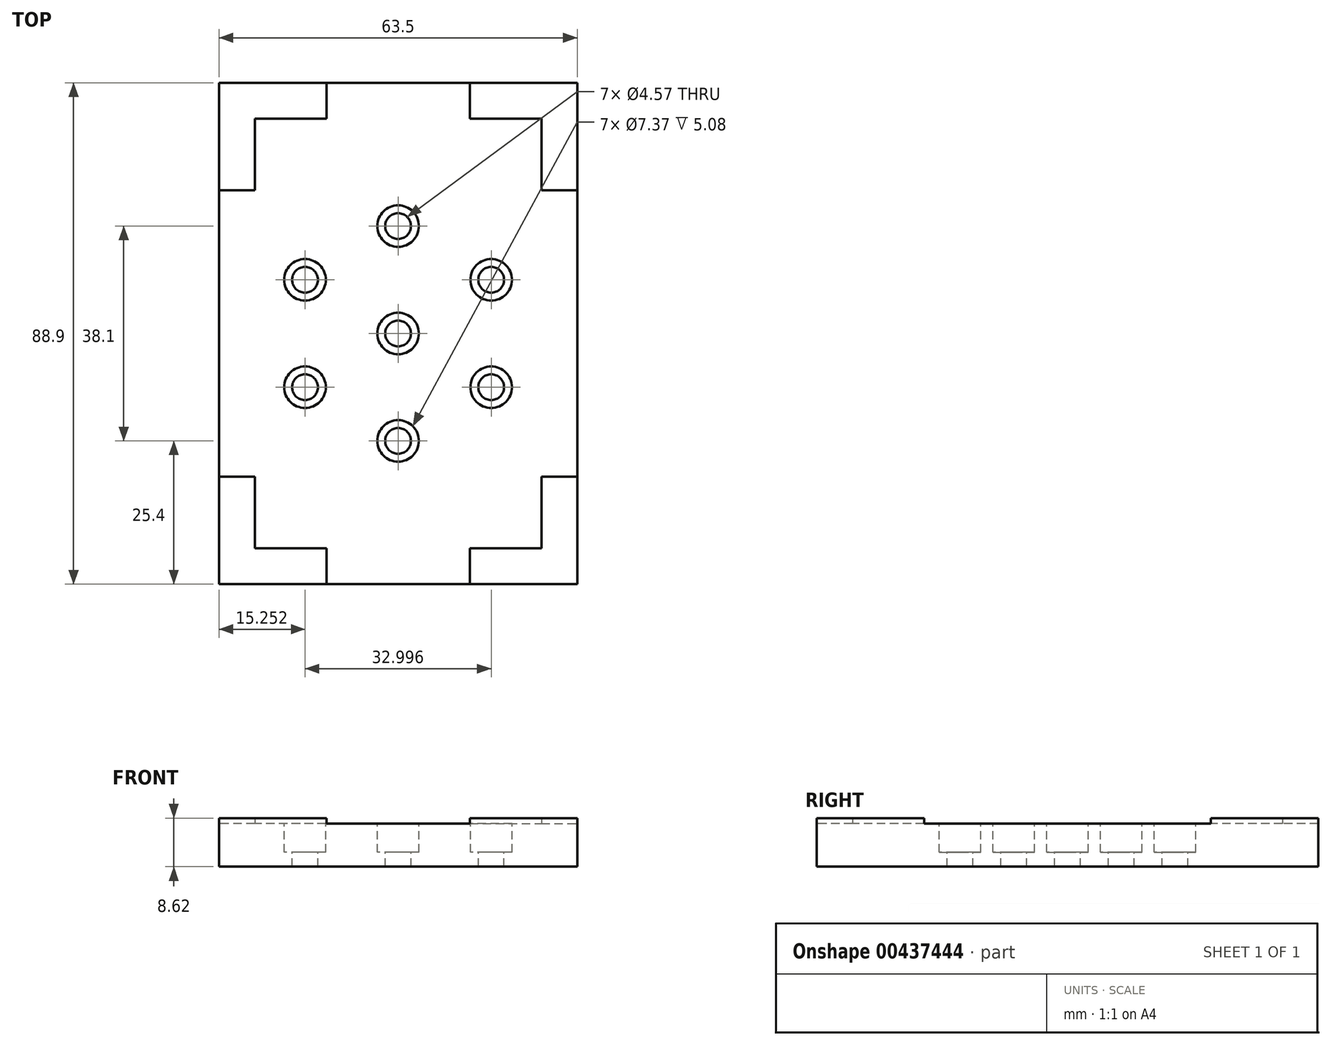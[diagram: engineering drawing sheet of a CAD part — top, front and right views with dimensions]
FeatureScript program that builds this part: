
annotation { "Feature Type Name" : "Feature", "Feature Type Description" : "" }
export const myFeature = defineFeature(function(context is Context, id is Id, definition is map)
    precondition{}
    {
        {
            var Q0;
            Q0=qCreatedBy(makeId("Top.planeOp"),FACE);
            var sketch = newSketch(context, id + "F0", { "sketchPlane" : qUnion([Q0])});
            skLineSegment(sketch, "E0.bottom", {"start": v(0, 0) * mm, "end": v(63.5, 0) * mm});
            skLineSegment(sketch, "E0.top", {"start": v(0, 88.9) * mm, "end": v(63.5, 88.9) * mm});
            skLineSegment(sketch, "E0.left", {"start": v(0, 0) * mm, "end": v(0, 88.9) * mm});
            skLineSegment(sketch, "E0.right", {"start": v(63.5, 0) * mm, "end": v(63.5, 88.9) * mm});
            skSolve(sketch);
        }
        {
            var Q0;
            Q0=makeQuery(id+"F0.imprint","IMPRINT",FACE,{"disambiguationData":[TD([[makeQuery(id+"F0.imprint","IMPRINT",EDGE,{"derivedFrom":sQuery(id+"F0.wireOp",EDGE,"E0.bottom")}),1.0]])]});
            extrude(context, id + "F1", {"entities" : qUnion([Q0]), "depth" : 7.62 * mm});
        }
        {
            var Q0;
            Q0=makeQuery(id+"F1.opExtrude","CAP_FACE",FACE,{"disambiguationData":[OSD([sQuery(id+"F0.wireOp",EDGE,"E0.bottom"),sQuery(id+"F0.wireOp",EDGE,"E0.top"),sQuery(id+"F0.wireOp",EDGE,"E0.left"),sQuery(id+"F0.wireOp",EDGE,"E0.right")])],"isStart":false});
            var sketch = newSketch(context, id + "F2", { "sketchPlane" : qUnion([Q0])});
            skCircle(sketch, "E1", {"center": v(31.75, 44.45) * mm, "radius": 2.29 * mm});
            skCircle(sketch, "E2", {"center": v(31.75, 63.5) * mm, "radius": 2.29 * mm});
            skCircle(sketch, "E3", {"center": v(31.75, 25.4) * mm, "radius": 2.29 * mm});
            skCircle(sketch, "E4", {"center": v(48.25, 34.92) * mm, "radius": 2.29 * mm});
            skCircle(sketch, "E5", {"center": v(48.25, 53.98) * mm, "radius": 2.29 * mm});
            skCircle(sketch, "E6", {"center": v(15.25, 53.98) * mm, "radius": 2.29 * mm});
            skCircle(sketch, "E7", {"center": v(15.25, 34.93) * mm, "radius": 2.29 * mm});
            skLineSegment(sketch, "E8", {"start": v(15.25, 34.93) * mm, "end": v(15.25, 53.98) * mm});
            skLineSegment(sketch, "E9", {"start": v(15.25, 53.98) * mm, "end": v(48.25, 53.98) * mm});
            skLineSegment(sketch, "E10", {"start": v(48.25, 34.92) * mm, "end": v(48.25, 53.98) * mm});
            skLineSegment(sketch, "E11", {"start": v(15.25, 34.93) * mm, "end": v(48.25, 34.93) * mm});
            skLineSegment(sketch, "E12", {"start": v(31.75, 44.45) * mm, "end": v(31.75, 63.5) * mm});
            skSolve(sketch);
        }
        {
            var Q0;
            Q0=makeQuery(id+"F2.imprint","IMPRINT",FACE,{"disambiguationData":[TD([[makeQuery(id+"F2.imprint","IMPRINT",EDGE,{"derivedFrom":sQuery(id+"F2.wireOp",EDGE,"E2")}),1.0]])]});
            var Q1;
            Q1=makeQuery(id+"F2.imprint","IMPRINT",FACE,{"disambiguationData":[TD([[makeQuery(id+"F2.imprint","IMPRINT",EDGE,{"derivedFrom":sQuery(id+"F2.wireOp",EDGE,"E3")}),1.0]])]});
            var Q2;
            {var subQ0=sQuery(id+"F2.wireOp",EDGE,"E10");var subQ1=sQuery(id+"F2.wireOp",EDGE,"E4");var subQ2=makeQuery(id+"F2.imprint","INTERSECT",VERTEX,{"derivedFrom":[subQ1,subQ0]});Q2=makeQuery(id+"F2.imprint","IMPRINT",FACE,{"disambiguationData":[TD([[makeQuery(id+"F2.imprint","IMPRINT",EDGE,{"disambiguationData":[TD([[subQ2,-1.0]])],"derivedFrom":subQ1}),1.0]])]});}
            var Q3;
            {var subQ0=sQuery(id+"F2.wireOp",EDGE,"E10");var subQ1=sQuery(id+"F2.wireOp",EDGE,"E4");var subQ2=makeQuery(id+"F2.imprint","INTERSECT",VERTEX,{"derivedFrom":[subQ1,subQ0]});Q3=makeQuery(id+"F2.imprint","IMPRINT",FACE,{"disambiguationData":[TD([[makeQuery(id+"F2.imprint","IMPRINT",EDGE,{"disambiguationData":[TD([[subQ2,1.0]])],"derivedFrom":subQ1}),1.0]])]});}
            var Q4;
            {var subQ0=sQuery(id+"F2.wireOp",EDGE,"E9");var subQ1=sQuery(id+"F2.wireOp",EDGE,"E5");var subQ2=makeQuery(id+"F2.imprint","INTERSECT",VERTEX,{"derivedFrom":[subQ1,subQ0]});Q4=makeQuery(id+"F2.imprint","IMPRINT",FACE,{"disambiguationData":[TD([[makeQuery(id+"F2.imprint","IMPRINT",EDGE,{"disambiguationData":[TD([[subQ2,-1.0]])],"derivedFrom":subQ1}),1.0]])]});}
            var Q5;
            {var subQ0=sQuery(id+"F2.wireOp",EDGE,"E9");var subQ1=sQuery(id+"F2.wireOp",EDGE,"E5");var subQ2=makeQuery(id+"F2.imprint","INTERSECT",VERTEX,{"derivedFrom":[subQ1,subQ0]});Q5=makeQuery(id+"F2.imprint","IMPRINT",FACE,{"disambiguationData":[TD([[makeQuery(id+"F2.imprint","IMPRINT",EDGE,{"disambiguationData":[TD([[subQ2,1.0]])],"derivedFrom":subQ1}),1.0]])]});}
            var Q6;
            {var subQ0=sQuery(id+"F2.wireOp",EDGE,"E8");var subQ1=sQuery(id+"F2.wireOp",EDGE,"E6");var subQ2=makeQuery(id+"F2.imprint","INTERSECT",VERTEX,{"derivedFrom":[subQ1,subQ0]});Q6=makeQuery(id+"F2.imprint","IMPRINT",FACE,{"disambiguationData":[TD([[makeQuery(id+"F2.imprint","IMPRINT",EDGE,{"disambiguationData":[TD([[subQ2,1.0]])],"derivedFrom":subQ1}),1.0]])]});}
            var Q7;
            {var subQ0=sQuery(id+"F2.wireOp",EDGE,"E8");var subQ1=sQuery(id+"F2.wireOp",EDGE,"E6");var subQ2=makeQuery(id+"F2.imprint","INTERSECT",VERTEX,{"derivedFrom":[subQ1,subQ0]});Q7=makeQuery(id+"F2.imprint","IMPRINT",FACE,{"disambiguationData":[TD([[makeQuery(id+"F2.imprint","IMPRINT",EDGE,{"disambiguationData":[TD([[subQ2,-1.0]])],"derivedFrom":subQ1}),1.0]])]});}
            var Q8;
            {var subQ0=sQuery(id+"F2.wireOp",EDGE,"E8");var subQ1=sQuery(id+"F2.wireOp",EDGE,"E7");var subQ2=makeQuery(id+"F2.imprint","INTERSECT",VERTEX,{"derivedFrom":[subQ1,subQ0]});Q8=makeQuery(id+"F2.imprint","IMPRINT",FACE,{"disambiguationData":[TD([[makeQuery(id+"F2.imprint","IMPRINT",EDGE,{"disambiguationData":[TD([[subQ2,1.0]])],"derivedFrom":subQ1}),1.0]])]});}
            var Q9;
            {var subQ0=sQuery(id+"F2.wireOp",EDGE,"E8");var subQ1=sQuery(id+"F2.wireOp",EDGE,"E7");var subQ2=makeQuery(id+"F2.imprint","INTERSECT",VERTEX,{"derivedFrom":[subQ1,subQ0]});Q9=makeQuery(id+"F2.imprint","IMPRINT",FACE,{"disambiguationData":[TD([[makeQuery(id+"F2.imprint","IMPRINT",EDGE,{"disambiguationData":[TD([[subQ2,-1.0]])],"derivedFrom":subQ1}),1.0]])]});}
            var Q10;
            Q10=makeQuery(id+"F2.imprint","IMPRINT",FACE,{"disambiguationData":[TD([[makeQuery(id+"F2.imprint","IMPRINT",EDGE,{"derivedFrom":sQuery(id+"F2.wireOp",EDGE,"E1")}),1.0]])]});
            extrude(context, id + "F3", {"entities" : qUnion([Q0, Q1, Q2, Q3, Q4, Q5, Q6, Q7, Q8, Q9, Q10]), "operationType" : NewBodyOperationType.REMOVE, "oppositeDirection" : true, "depth" : 25.4 * mm});
        }
        {
            var Q0;
            Q0=makeQuery(id+"F1.opExtrude","CAP_FACE",FACE,{"disambiguationData":[OSD([sQuery(id+"F0.wireOp",EDGE,"E0.bottom"),sQuery(id+"F0.wireOp",EDGE,"E0.top"),sQuery(id+"F0.wireOp",EDGE,"E0.left"),sQuery(id+"F0.wireOp",EDGE,"E0.right")])],"isStart":false});
            var sketch = newSketch(context, id + "F4", { "sketchPlane" : qUnion([Q0])});
            skCircle(sketch, "E13", {"center": v(15.25, 34.93) * mm, "radius": 3.68 * mm});
            skCircle(sketch, "E14", {"center": v(15.25, 53.98) * mm, "radius": 3.68 * mm});
            skCircle(sketch, "E15", {"center": v(31.75, 63.5) * mm, "radius": 3.68 * mm});
            skCircle(sketch, "E16", {"center": v(48.25, 53.98) * mm, "radius": 3.68 * mm});
            skCircle(sketch, "E17", {"center": v(48.25, 34.92) * mm, "radius": 3.68 * mm});
            skCircle(sketch, "E18", {"center": v(31.75, 25.4) * mm, "radius": 3.68 * mm});
            skCircle(sketch, "E19", {"center": v(31.75, 44.45) * mm, "radius": 3.68 * mm});
            skSolve(sketch);
        }
        {
            var Q0;
            Q0=makeQuery(id+"F4.imprint","IMPRINT",FACE,{"disambiguationData":[TD([[makeQuery(id+"F4.imprint","IMPRINT",EDGE,{"derivedFrom":sQuery(id+"F4.wireOp",EDGE,"E13")}),1.0]])]});
            var Q1;
            Q1=makeQuery(id+"F4.imprint","IMPRINT",FACE,{"disambiguationData":[TD([[makeQuery(id+"F4.imprint","IMPRINT",EDGE,{"derivedFrom":sQuery(id+"F4.wireOp",EDGE,"E14")}),1.0]])]});
            var Q2;
            Q2=makeQuery(id+"F4.imprint","IMPRINT",FACE,{"disambiguationData":[TD([[makeQuery(id+"F4.imprint","IMPRINT",EDGE,{"derivedFrom":sQuery(id+"F4.wireOp",EDGE,"E15")}),1.0]])]});
            var Q3;
            Q3=makeQuery(id+"F4.imprint","IMPRINT",FACE,{"disambiguationData":[TD([[makeQuery(id+"F4.imprint","IMPRINT",EDGE,{"derivedFrom":sQuery(id+"F4.wireOp",EDGE,"E16")}),1.0]])]});
            var Q4;
            Q4=makeQuery(id+"F4.imprint","IMPRINT",FACE,{"disambiguationData":[TD([[makeQuery(id+"F4.imprint","IMPRINT",EDGE,{"derivedFrom":sQuery(id+"F4.wireOp",EDGE,"E17")}),1.0]])]});
            var Q5;
            Q5=makeQuery(id+"F4.imprint","IMPRINT",FACE,{"disambiguationData":[TD([[makeQuery(id+"F4.imprint","IMPRINT",EDGE,{"derivedFrom":sQuery(id+"F4.wireOp",EDGE,"E18")}),1.0]])]});
            var Q6;
            Q6=makeQuery(id+"F4.imprint","IMPRINT",FACE,{"disambiguationData":[TD([[makeQuery(id+"F4.imprint","IMPRINT",EDGE,{"derivedFrom":sQuery(id+"F4.wireOp",EDGE,"E19")}),1.0]])]});
            extrude(context, id + "F5", {"entities" : qUnion([Q0, Q1, Q2, Q3, Q4, Q5, Q6]), "operationType" : NewBodyOperationType.REMOVE, "oppositeDirection" : true, "depth" : 5.08 * mm});
        }
        {
            var Q0;
            Q0=makeQuery(id+"F1.opExtrude","CAP_FACE",FACE,{"disambiguationData":[OSD([sQuery(id+"F0.wireOp",EDGE,"E0.bottom"),sQuery(id+"F0.wireOp",EDGE,"E0.top"),sQuery(id+"F0.wireOp",EDGE,"E0.left"),sQuery(id+"F0.wireOp",EDGE,"E0.right")])],"isStart":false});
            var sketch = newSketch(context, id + "F6", { "sketchPlane" : qUnion([Q0])});
            skLineSegment(sketch, "E20", {"start": v(0, 19.05) * mm, "end": v(6.35, 19.05) * mm});
            skLineSegment(sketch, "E21", {"start": v(6.35, 19.05) * mm, "end": v(6.35, 6.35) * mm});
            skLineSegment(sketch, "E22", {"start": v(6.35, 6.35) * mm, "end": v(19.05, 6.35) * mm});
            skLineSegment(sketch, "E23", {"start": v(19.05, 6.35) * mm, "end": v(19.05, 0) * mm});
            skLineSegment(sketch, "E24", {"start": v(19.05, 0) * mm, "end": v(44.45, 0) * mm});
            skLineSegment(sketch, "E25", {"start": v(44.45, 0) * mm, "end": v(44.45, 6.35) * mm});
            skLineSegment(sketch, "E26", {"start": v(44.45, 6.35) * mm, "end": v(57.15, 6.35) * mm});
            skLineSegment(sketch, "E27", {"start": v(57.15, 6.35) * mm, "end": v(57.15, 19.05) * mm});
            skLineSegment(sketch, "E28", {"start": v(57.15, 19.05) * mm, "end": v(63.5, 19.05) * mm});
            skLineSegment(sketch, "E29", {"start": v(63.5, 19.05) * mm, "end": v(63.5, 69.85) * mm});
            skLineSegment(sketch, "E30", {"start": v(63.5, 69.85) * mm, "end": v(57.15, 69.85) * mm});
            skLineSegment(sketch, "E31", {"start": v(57.15, 69.85) * mm, "end": v(57.15, 82.55) * mm});
            skLineSegment(sketch, "E32", {"start": v(57.15, 82.55) * mm, "end": v(44.45, 82.55) * mm});
            skLineSegment(sketch, "E33", {"start": v(44.45, 82.55) * mm, "end": v(44.45, 88.9) * mm});
            skLineSegment(sketch, "E34", {"start": v(44.45, 88.9) * mm, "end": v(19.05, 88.9) * mm});
            skLineSegment(sketch, "E35", {"start": v(19.05, 88.9) * mm, "end": v(19.05, 82.55) * mm});
            skLineSegment(sketch, "E36", {"start": v(19.05, 82.55) * mm, "end": v(6.35, 82.55) * mm});
            skLineSegment(sketch, "E37", {"start": v(6.35, 82.55) * mm, "end": v(6.35, 69.85) * mm});
            skLineSegment(sketch, "E38", {"start": v(6.35, 69.85) * mm, "end": v(0, 69.85) * mm});
            skLineSegment(sketch, "E39", {"start": v(0, 69.85) * mm, "end": v(0, 19.05) * mm});
            skSolve(sketch);
        }
        {
            var Q0;
            {var subQ1=sQuery(id+"F6.wireOp",EDGE,"E20");Q0=makeQuery(id+"F6.imprint","IMPRINT",FACE,{"disambiguationData":[TD([[makeQuery(id+"F6.imprint","IMPRINT",EDGE,{"derivedFrom":subQ1}),-1.0]])]});}
            var Q1;
            {var subQ1=sQuery(id+"F6.wireOp",EDGE,"E25");Q1=makeQuery(id+"F6.imprint","IMPRINT",FACE,{"disambiguationData":[TD([[makeQuery(id+"F6.imprint","IMPRINT",EDGE,{"derivedFrom":subQ1}),-1.0]])]});}
            var Q2;
            {var subQ4=sQuery(id+"F6.wireOp",EDGE,"E30");Q2=makeQuery(id+"F6.imprint","IMPRINT",FACE,{"disambiguationData":[TD([[makeQuery(id+"F6.imprint","IMPRINT",EDGE,{"derivedFrom":subQ4}),-1.0]])]});}
            var Q3;
            {var subQ4=sQuery(id+"F6.wireOp",EDGE,"E35");Q3=makeQuery(id+"F6.imprint","IMPRINT",FACE,{"disambiguationData":[TD([[makeQuery(id+"F6.imprint","IMPRINT",EDGE,{"derivedFrom":subQ4}),-1.0]])]});}
            extrude(context, id + "F7", {"entities" : qUnion([Q0, Q1, Q2, Q3]), "operationType" : NewBodyOperationType.ADD, "depth" : 1 * mm});
        }
    });
